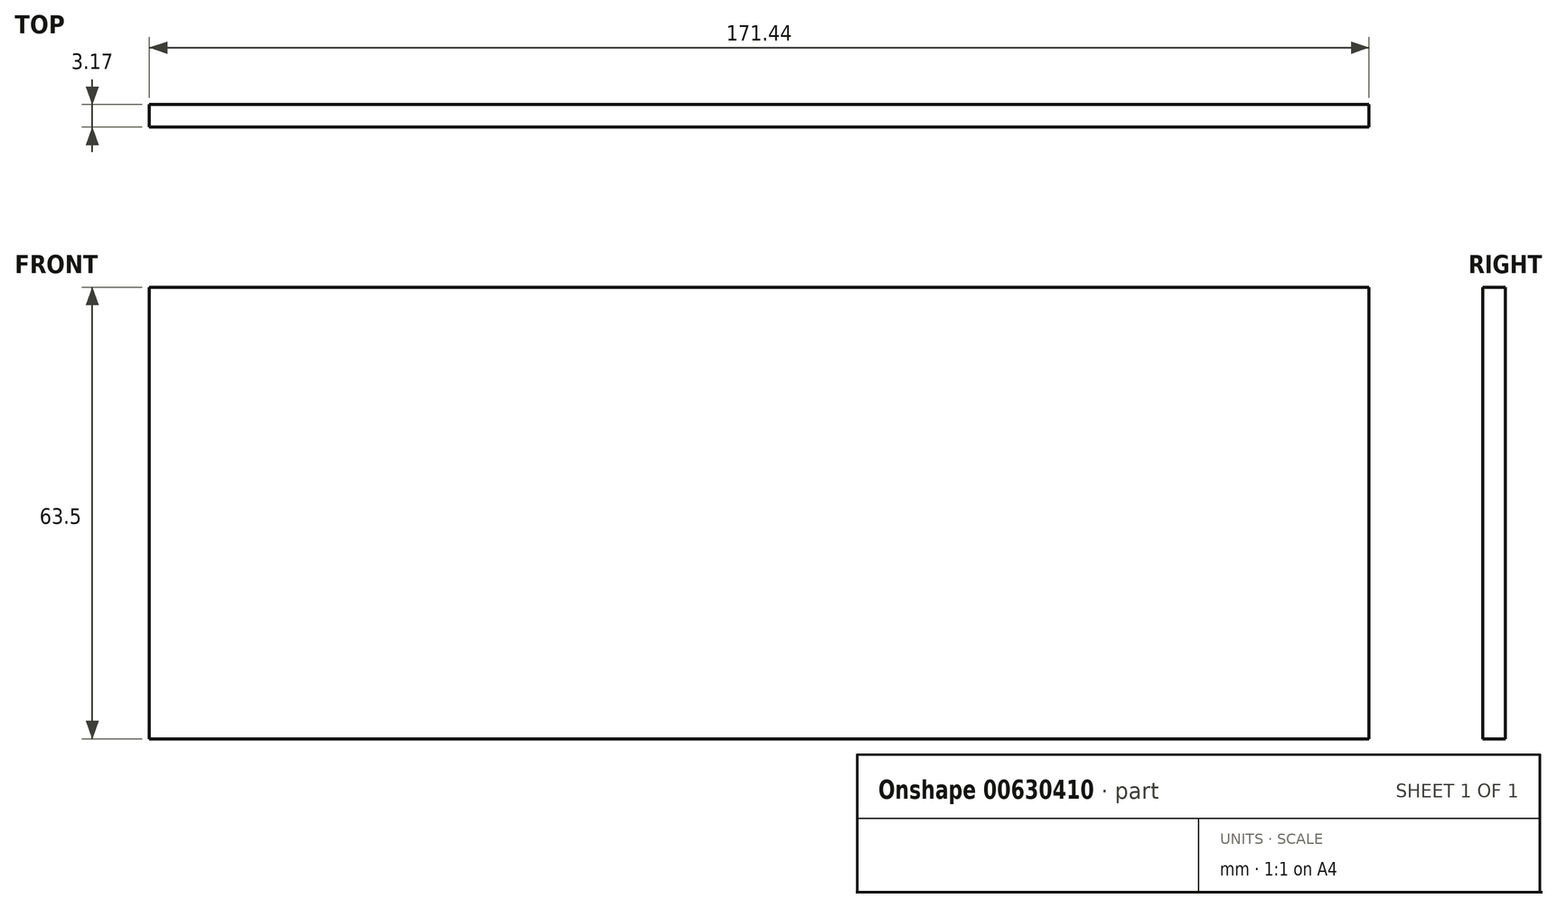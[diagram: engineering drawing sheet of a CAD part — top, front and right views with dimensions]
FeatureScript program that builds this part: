
annotation { "Feature Type Name" : "Feature", "Feature Type Description" : "" }
export const myFeature = defineFeature(function(context is Context, id is Id, definition is map)
    precondition{}
    {
        {
            var Q0;
            Q0=qCreatedBy(makeId("Front.planeOp"),FACE);
            var sketch = newSketch(context, id + "F0", { "sketchPlane" : qUnion([Q0])});
            skLineSegment(sketch, "E0.bottom", {"start": v(85.73, 31.75) * mm, "end": v(-85.72, 31.75) * mm});
            skLineSegment(sketch, "E0.top", {"start": v(85.72, -31.75) * mm, "end": v(-85.73, -31.75) * mm});
            skLineSegment(sketch, "E0.left", {"start": v(85.73, 31.75) * mm, "end": v(85.72, -31.75) * mm});
            skLineSegment(sketch, "E0.right", {"start": v(-85.72, 31.75) * mm, "end": v(-85.73, -31.75) * mm});
            skPoint(sketch, "E0.middle", {"position": v(0, 0) * mm});
            skSolve(sketch);
        }
        {
            var Q0;
            Q0 = qSketchRegion(id + "F0", true);
            extrude(context, id + "F1", {"entities" : qUnion([Q0]), "depth" : 3.17 * mm, "offsetDistance" : 25.4 * mm});
        }
    });
